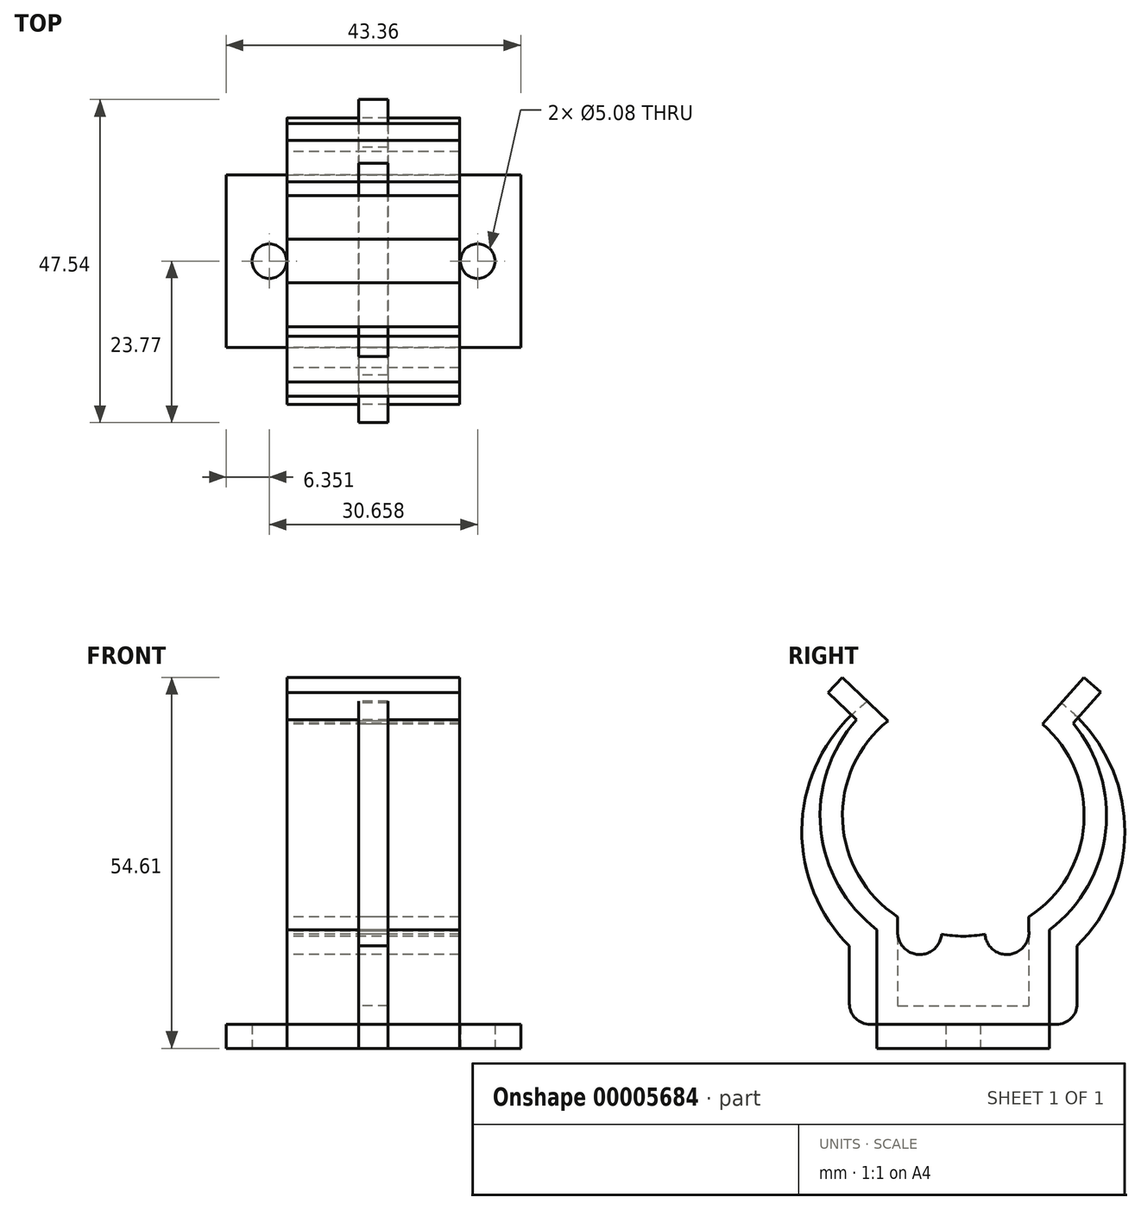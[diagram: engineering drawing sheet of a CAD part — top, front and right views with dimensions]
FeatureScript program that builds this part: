
annotation { "Feature Type Name" : "Feature", "Feature Type Description" : "" }
export const myFeature = defineFeature(function(context is Context, id is Id, definition is map)
    precondition{}
    {
        {
            var Q0;
            Q0=qCreatedBy(makeId("Top.planeOp"),FACE);
            var sketch = newSketch(context, id + "F0", { "sketchPlane" : qUnion([Q0])});
            skLineSegment(sketch, "E0.bottom", {"start": v(-21.68, 12.7) * mm, "end": v(21.68, 12.7) * mm, "construction": true});
            skLineSegment(sketch, "E0.top", {"start": v(-21.68, -12.7) * mm, "end": v(21.68, -12.7) * mm, "construction": true});
            skLineSegment(sketch, "E0.left", {"start": v(-21.68, 12.7) * mm, "end": v(-21.68, -12.7) * mm, "construction": true});
            skLineSegment(sketch, "E0.right", {"start": v(21.68, 12.7) * mm, "end": v(21.68, -12.7) * mm, "construction": true});
            skLineSegment(sketch, "E1", {"start": v(0, 32.62) * mm, "end": v(21.68, 32.62) * mm, "construction": true});
            skLineSegment(sketch, "E2", {"start": v(54.05, 0) * mm, "end": v(54.05, -12.7) * mm, "construction": true});
            skLineSegment(sketch, "E3.bottom", {"start": v(-21.68, 12.7) * mm, "end": v(21.68, 12.7) * mm});
            skLineSegment(sketch, "E3.top", {"start": v(-21.68, -12.7) * mm, "end": v(21.68, -12.7) * mm});
            skLineSegment(sketch, "E3.left", {"start": v(-21.68, 12.7) * mm, "end": v(-21.68, -12.7) * mm});
            skLineSegment(sketch, "E3.right", {"start": v(21.68, 12.7) * mm, "end": v(21.68, -12.7) * mm});
            skLineSegment(sketch, "E4", {"start": v(-21.68, 49.39) * mm, "end": v(-15.33, 49.39) * mm, "construction": true});
            skLineSegment(sketch, "E5", {"start": v(21.68, 72.87) * mm, "end": v(15.33, 72.87) * mm, "construction": true});
            skCircle(sketch, "E6", {"center": v(-15.33, 0) * mm, "radius": 2.54 * mm});
            skCircle(sketch, "E7", {"center": v(15.33, 0) * mm, "radius": 2.54 * mm});
            skSolve(sketch);
        }
        {
            var Q0;
            Q0=makeQuery(id+"F0.imprint","IMPRINT",FACE,{"disambiguationData":[TD([[makeQuery(id+"F0.imprint","IMPRINT",EDGE,{"derivedFrom":sQuery(id+"F0.wireOp",EDGE,"E3.bottom")}),-1.0]])]});
            extrude(context, id + "F1", {"entities" : qUnion([Q0]), "depth" : 3.56 * mm});
        }
        {
            var Q0;
            Q0=qCreatedBy(makeId("Right.planeOp"),FACE);
            var sketch = newSketch(context, id + "F2", { "sketchPlane" : qUnion([Q0])});
            skLineSegment(sketch, "E8", {"start": v(0, 0) * mm, "end": v(0, 34.3) * mm, "construction": true});
            skLineSegment(sketch, "E9", {"start": v(-27.6, 34.3) * mm, "end": v(-27.6, 16.51) * mm, "construction": true});
            skArc(sketch, "E10", {"start": v(-11.07, 48.2) * mm, "mid": v(-17.76, 33.42) * mm, "end": v(-9.65, 19.36) * mm});
            skLineSegment(sketch, "E11", {"start": v(66.9, 0) * mm, "end": v(66.9, 54.61) * mm, "construction": true});
            skLineSegment(sketch, "E12", {"start": v(17.78, 54.61) * mm, "end": v(11.65, 47.73) * mm});
            skLineSegment(sketch, "E13", {"start": v(17.78, 65.84) * mm, "end": v(0, 65.84) * mm, "construction": true});
            skLineSegment(sketch, "E14", {"start": v(0, 65.84) * mm, "end": v(-17.78, 65.84) * mm, "construction": true});
            skLineSegment(sketch, "E15", {"start": v(-17.78, 54.61) * mm, "end": v(-11.07, 48.2) * mm});
            skLineSegment(sketch, "E16", {"start": v(17.78, 54.61) * mm, "end": v(20.22, 52.44) * mm});
            skLineSegment(sketch, "E17", {"start": v(-17.78, 54.61) * mm, "end": v(-19.92, 52.37) * mm});
            skLineSegment(sketch, "E18.rect.bottom", {"start": v(3.2, 0) * mm, "end": v(-3.2, 0) * mm});
            skLineSegment(sketch, "E18.rect.left", {"start": v(3.2, 16.8) * mm, "end": v(3.2, 16.8) * mm});
            skLineSegment(sketch, "E18.rect.right", {"start": v(-3.2, 16.8) * mm, "end": v(-3.2, 16.8) * mm});
            skPoint(sketch, "E18.rect.middle", {"position": v(0, 8.5) * mm});
            skLineSegment(sketch, "E19.top", {"start": v(-11.07, 0) * mm, "end": v(-8.02, 0) * mm});
            skLineSegment(sketch, "E20.top", {"start": v(11.65, 0) * mm, "end": v(8.6, 0) * mm});
            skLineSegment(sketch, "E21.bottom", {"start": v(11.65, 0) * mm, "end": v(-11.07, 0) * mm});
            skArc(sketch, "E22.trimOffspring", {"start": v(12.7, 17.46) * mm, "mid": v(20.95, 31.92) * mm, "end": v(16.14, 47.86) * mm});
            skLineSegment(sketch, "E23", {"start": v(12.7, -11.08) * mm, "end": v(0, -11.08) * mm});
            skLineSegment(sketch, "E24", {"start": v(0, -11.08) * mm, "end": v(-12.7, -11.08) * mm});
            skLineSegment(sketch, "E25.bottom", {"start": v(12.7, 0) * mm, "end": v(-12.7, 0) * mm});
            skLineSegment(sketch, "E25.left", {"start": v(12.7, 0) * mm, "end": v(12.7, 3.57) * mm});
            skLineSegment(sketch, "E25.right", {"start": v(-12.7, 0) * mm, "end": v(-12.7, 3.57) * mm});
            skLineSegment(sketch, "E26.left", {"start": v(12.7, 3.57) * mm, "end": v(12.7, 17.46) * mm});
            skLineSegment(sketch, "E26.right", {"start": v(9.65, 16.8) * mm, "end": v(9.65, 19.36) * mm});
            skLineSegment(sketch, "E27.left", {"start": v(-12.7, 3.57) * mm, "end": v(-12.7, 17.46) * mm});
            skLineSegment(sketch, "E27.right", {"start": v(-9.65, 16.8) * mm, "end": v(-9.65, 19.36) * mm});
            skArc(sketch, "E28", {"start": v(-3.2, 16.8) * mm, "mid": v(0, 16.51) * mm, "end": v(3.2, 16.8) * mm});
            skArc(sketch, "E29", {"start": v(9.65, 19.36) * mm, "mid": v(17.74, 33.04) * mm, "end": v(11.65, 47.73) * mm});
            skLineSegment(sketch, "E30", {"start": v(-19.92, 52.37) * mm, "end": v(-19.92, 52.37) * mm});
            skLineSegment(sketch, "E31", {"start": v(20.22, 52.44) * mm, "end": v(16.14, 47.86) * mm});
            skLineSegment(sketch, "E32", {"start": v(16.14, 47.86) * mm, "end": v(16.14, 47.86) * mm});
            skLineSegment(sketch, "E33", {"start": v(-19.92, 52.37) * mm, "end": v(-15.7, 48.35) * mm});
            skArc(sketch, "E34", {"start": v(-15.7, 48.35) * mm, "mid": v(-20.98, 32.25) * mm, "end": v(-12.7, 17.46) * mm});
            skArc(sketch, "E35", {"start": v(-9.66, 17) * mm, "mid": v(-6.52, 13.8) * mm, "end": v(-3.2, 16.8) * mm});
            skArc(sketch, "E36", {"start": v(-9.65, 17.28) * mm, "mid": v(-9.66, 17.14) * mm, "end": v(-9.66, 17) * mm});
            skArc(sketch, "E37", {"start": v(3.2, 16.8) * mm, "mid": v(6.63, 13.8) * mm, "end": v(9.66, 17.22) * mm});
            skArc(sketch, "E38", {"start": v(9.66, 17.22) * mm, "mid": v(9.65, 17.25) * mm, "end": v(9.65, 17.28) * mm});
            skSolve(sketch);
        }
        {
            var Q0;
            {var subQ11=sQuery(id+"F2.wireOp",EDGE,"E10");Q0=makeQuery(id+"F2.imprint","IMPRINT",FACE,{"disambiguationData":[TD([[makeQuery(id+"F2.imprint","IMPRINT",EDGE,{"derivedFrom":subQ11}),-1.0]])]});}
            extrude(context, id + "F3", {"entities" : qUnion([Q0]), "endBound" : BoundingType.SYMMETRIC, "depth" : 25.4 * mm});
        }
        {
            var Q0;
            Q0=qCreatedBy(makeId("Right.planeOp"),FACE);
            var sketch = newSketch(context, id + "F4", { "sketchPlane" : qUnion([Q0])});
            skArc(sketch, "E39.0.0", {"start": v(-11.07, 48.2) * mm, "mid": v(-17.76, 33.42) * mm, "end": v(-9.65, 19.36) * mm});
            skLineSegment(sketch, "E39.0.1", {"start": v(-14.09, 51.09) * mm, "end": v(-11.07, 48.2) * mm});
            skLineSegment(sketch, "E39.0.3", {"start": v(-16.47, 49.08) * mm, "end": v(-16.46, 49.06) * mm});
            skLineSegment(sketch, "E39.0.5", {"start": v(-12.7, 0) * mm, "end": v(-12.7, 3.52) * mm});
            skLineSegment(sketch, "E39.0.6", {"start": v(12.7, 0) * mm, "end": v(-12.7, 0) * mm});
            skLineSegment(sketch, "E39.0.7", {"start": v(12.7, 0) * mm, "end": v(12.7, 3.52) * mm});
            skLineSegment(sketch, "E39.0.9", {"start": v(16.88, 48.69) * mm, "end": v(16.86, 48.67) * mm});
            skLineSegment(sketch, "E39.0.11", {"start": v(14.42, 50.84) * mm, "end": v(11.65, 47.73) * mm});
            skArc(sketch, "E39.0.12", {"start": v(9.65, 19.36) * mm, "mid": v(17.74, 33.04) * mm, "end": v(11.65, 47.73) * mm});
            skLineSegment(sketch, "E39.0.13", {"start": v(9.65, 17.28) * mm, "end": v(9.65, 19.36) * mm});
            skArc(sketch, "E39.0.14", {"start": v(9.65, 16.8) * mm, "mid": v(9.66, 17.04) * mm, "end": v(9.65, 17.28) * mm});
            skArc(sketch, "E39.0.16", {"start": v(-9.65, 17.28) * mm, "mid": v(-9.66, 17.04) * mm, "end": v(-9.65, 16.8) * mm});
            skLineSegment(sketch, "E39.0.17", {"start": v(-9.65, 17.28) * mm, "end": v(-9.65, 19.36) * mm});
            skArc(sketch, "E40", {"start": v(-14.09, 51.09) * mm, "mid": v(-15.31, 50.12) * mm, "end": v(-16.47, 49.08) * mm});
            skLineSegment(sketch, "E41.top", {"start": v(-12.7, 3.52) * mm, "end": v(-13.72, 3.52) * mm});
            skLineSegment(sketch, "E41.right", {"start": v(-16.76, 15.07) * mm, "end": v(-16.76, 6.57) * mm});
            skLineSegment(sketch, "E42.top", {"start": v(12.7, 3.52) * mm, "end": v(13.72, 3.52) * mm});
            skLineSegment(sketch, "E42.right", {"start": v(16.76, 15.07) * mm, "end": v(16.76, 6.57) * mm});
            skPoint(sketch, "E43.visualSharp", {"position": v(-16.76, 3.52) * mm});
            skArc(sketch, "E43.filletArc", {"start": v(-16.76, 6.57) * mm, "mid": v(-15.87, 4.41) * mm, "end": v(-13.72, 3.52) * mm});
            skPoint(sketch, "E44.visualSharp", {"position": v(16.76, 3.52) * mm});
            skArc(sketch, "E44.filletArc", {"start": v(13.72, 3.52) * mm, "mid": v(15.87, 4.41) * mm, "end": v(16.76, 6.57) * mm});
            skArc(sketch, "E45.trimOffspring", {"start": v(16.88, 48.69) * mm, "mid": v(15.69, 49.8) * mm, "end": v(14.42, 50.84) * mm});
            skArc(sketch, "E46", {"start": v(-14.07, 51.07) * mm, "mid": v(-23.7, 33.69) * mm, "end": v(-16.76, 15.07) * mm});
            skArc(sketch, "E47", {"start": v(16.76, 15.07) * mm, "mid": v(23.72, 33.48) * mm, "end": v(14.4, 50.82) * mm});
            skLineSegment(sketch, "E48.top", {"start": v(-9.65, 6.23) * mm, "end": v(9.65, 6.23) * mm});
            skLineSegment(sketch, "E48.left", {"start": v(-9.65, 19.36) * mm, "end": v(-9.65, 6.23) * mm});
            skLineSegment(sketch, "E48.right", {"start": v(9.65, 19.36) * mm, "end": v(9.65, 6.23) * mm});
            skSolve(sketch);
        }
        {
            var Q0;
            {var subQ3=sQuery(id+"F4.wireOp",EDGE,"E39.0.0");Q0=makeQuery(id+"F4.imprint","IMPRINT",FACE,{"disambiguationData":[TD([[makeQuery(id+"F4.imprint","IMPRINT",EDGE,{"derivedFrom":subQ3}),-1.0]])]});}
            extrude(context, id + "F5", {"entities" : qUnion([Q0]), "endBound" : BoundingType.SYMMETRIC, "depth" : 4.32 * mm});
        }
    });
